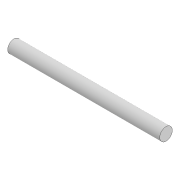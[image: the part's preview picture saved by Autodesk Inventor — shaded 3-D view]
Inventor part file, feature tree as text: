
AUTODESK INVENTOR PART (.ipt)
format: ipt  version: 2021 (Build 250183000, 183)  size: 73,728 bytes
history: native  units: in
note: dims shown in document units (in); Inventor stores cm internally (conversion verified against a paired STEP export)
features: extrude x1, sketch x1
ambient origin geometry x8: Origin, YZ Plane, XZ Plane, XY Plane, X Axis, Y Axis, Z Axis, Center Point
bodies: Solid1 (feature_tree)
feature tree (2):
  extrude  "Extrusion1"  Depth=2.3622in TaperAngle=0.0deg
  sketch  "Sketch1"  dims[d0=0.1969in d1=2.3622in d2=0.0in d3=0.5in d4=0.0344in d5=0.5in d6=0.0344in]
